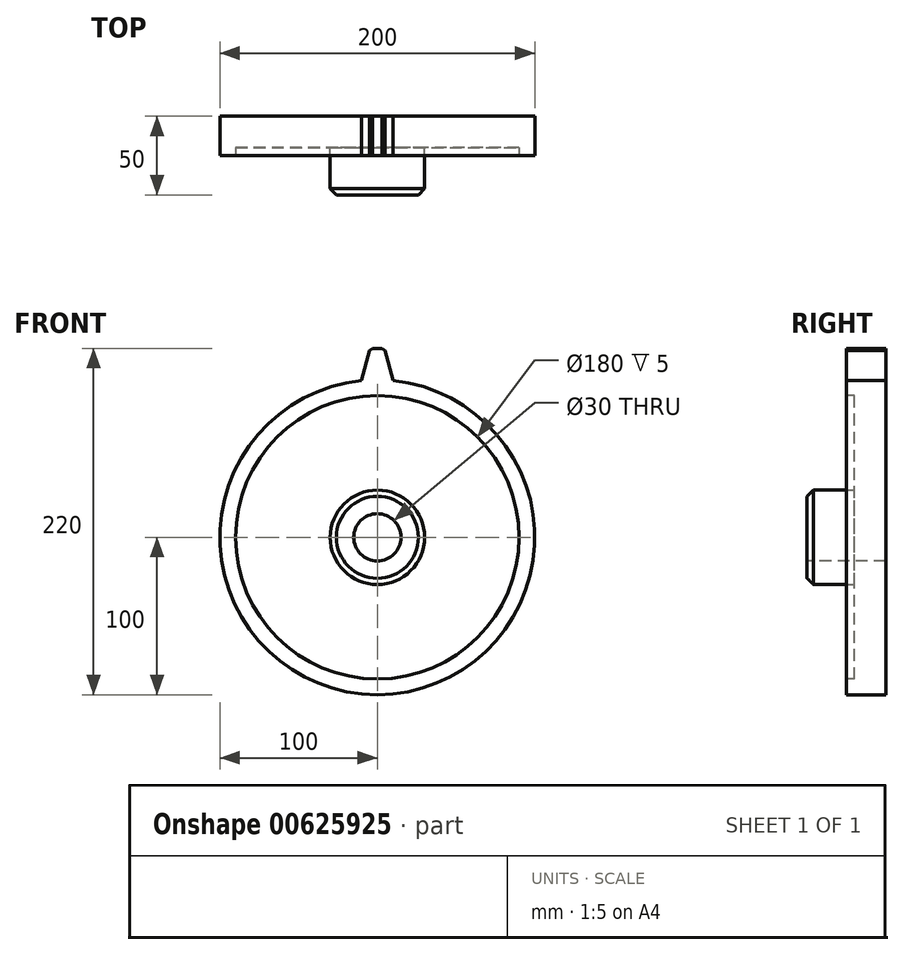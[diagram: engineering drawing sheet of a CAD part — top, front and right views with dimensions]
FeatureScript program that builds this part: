
annotation { "Feature Type Name" : "Feature", "Feature Type Description" : "" }
export const myFeature = defineFeature(function(context is Context, id is Id, definition is map)
    precondition{}
    {
        {
            var Q0;
            Q0=qCreatedBy(makeId("Front.planeOp"),FACE);
            var sketch = newSketch(context, id + "F0", { "sketchPlane" : qUnion([Q0])});
            skCircle(sketch, "E0", {"center": v(0, 0) * mm, "radius": 100 * mm});
            skSolve(sketch);
        }
        {
            var Q0;
            Q0=makeQuery(id+"F0.imprint","IMPRINT",FACE,{"disambiguationData":[TD([[makeQuery(id+"F0.imprint","IMPRINT",EDGE,{"derivedFrom":sQuery(id+"F0.wireOp",EDGE,"E0")}),1.0]])]});
            extrude(context, id + "F1", {"entities" : qUnion([Q0]), "depth" : 25 * mm, "offsetDistance" : 25 * mm});
        }
        {
            var Q0;
            Q0=qCreatedBy(makeId("Front.planeOp"),FACE);
            var sketch = newSketch(context, id + "F2", { "sketchPlane" : qUnion([Q0])});
            skLineSegment(sketch, "E1", {"start": v(-10, 99.5) * mm, "end": v(10, 99.5) * mm});
            skLineSegment(sketch, "E2", {"start": v(10, 99.5) * mm, "end": v(4.5, 120) * mm});
            skLineSegment(sketch, "E3", {"start": v(-4.5, 120) * mm, "end": v(4.5, 120) * mm});
            skLineSegment(sketch, "E4", {"start": v(-4.5, 120) * mm, "end": v(-10, 99.5) * mm});
            skSolve(sketch);
        }
        {
            var Q0;
            Q0 = qSketchRegion(id + "F2", true);
            extrude(context, id + "F3", {"entities" : qUnion([Q0]), "operationType" : NewBodyOperationType.ADD, "depth" : 25 * mm, "offsetDistance" : 25 * mm});
        }
        {
            var Q0;
            Q0=makeQuery(id+"F3.opExtrude","SWEPT_EDGE",EDGE,{"disambiguationData":[OSD([sQuery(id+"F2.wireOp",EDGE,"E3"),sQuery(id+"F2.wireOp",EDGE,"E4")])]});
            var Q1;
            Q1=makeQuery(id+"F3.opExtrude","SWEPT_EDGE",EDGE,{"disambiguationData":[OSD([sQuery(id+"F2.wireOp",EDGE,"E2"),sQuery(id+"F2.wireOp",EDGE,"E3")])]});
            chamfer(context, id + "F4", {"entities" : qUnion([Q0, Q1]), "width" : 2 * mm, "tangentPropagation" : true});
        }
        {
            var Q0;
            Q0=makeQuery(id+"F3.opExtrude","SWEPT_EDGE",EDGE,{"disambiguationData":[OSD([sQuery(id+"F2.wireOp",EDGE,"E1"),sQuery(id+"F2.wireOp",EDGE,"E2")])]});
            var Q1;
            Q1=makeQuery(id+"F3.opExtrude","SWEPT_EDGE",EDGE,{"disambiguationData":[OSD([sQuery(id+"F2.wireOp",EDGE,"E1"),sQuery(id+"F2.wireOp",EDGE,"E4")])]});
            fillet(context, id + "F5", {"entities" : qUnion([Q0, Q1]), "radius" : 5 * mm, "tangentPropagation" : true, "allowEdgeOverflow" : false});
        }
        {
            var Q0;
            {var subQ0=sQuery(id+"F2.wireOp",EDGE,"E4");var subQ1=sQuery(id+"F2.wireOp",EDGE,"E3");var subQ2=sQuery(id+"F2.wireOp",EDGE,"E2");var subQ3=sQuery(id+"F2.wireOp",EDGE,"E1");Q0=makeQuery(id+"FsMtaJyEFqotJcS_1.19.F3.boolean.opBoolean","MERGE",FACE,{"derivedFrom":[makeQuery(id+"FsMtaJyEFqotJcS_1.18.F3.boolean.opBoolean","MERGE",FACE,{"derivedFrom":[makeQuery(id+"FsMtaJyEFqotJcS_1.17.F3.boolean.opBoolean","MERGE",FACE,{"derivedFrom":[makeQuery(id+"FsMtaJyEFqotJcS_1.16.F3.boolean.opBoolean","MERGE",FACE,{"derivedFrom":[makeQuery(id+"FsMtaJyEFqotJcS_1.15.F3.boolean.opBoolean","MERGE",FACE,{"derivedFrom":[makeQuery(id+"FsMtaJyEFqotJcS_1.14.F3.boolean.opBoolean","MERGE",FACE,{"derivedFrom":[makeQuery(id+"FsMtaJyEFqotJcS_1.13.F3.boolean.opBoolean","MERGE",FACE,{"derivedFrom":[makeQuery(id+"FsMtaJyEFqotJcS_1.12.F3.boolean.opBoolean","MERGE",FACE,{"derivedFrom":[makeQuery(id+"FsMtaJyEFqotJcS_1.11.F3.boolean.opBoolean","MERGE",FACE,{"derivedFrom":[makeQuery(id+"FsMtaJyEFqotJcS_1.10.F3.boolean.opBoolean","MERGE",FACE,{"derivedFrom":[makeQuery(id+"FsMtaJyEFqotJcS_1.9.F3.boolean.opBoolean","MERGE",FACE,{"derivedFrom":[makeQuery(id+"FsMtaJyEFqotJcS_1.8.F3.boolean.opBoolean","MERGE",FACE,{"derivedFrom":[makeQuery(id+"FsMtaJyEFqotJcS_1.7.F3.boolean.opBoolean","MERGE",FACE,{"derivedFrom":[makeQuery(id+"FsMtaJyEFqotJcS_1.6.F3.boolean.opBoolean","MERGE",FACE,{"derivedFrom":[makeQuery(id+"FsMtaJyEFqotJcS_1.5.F3.boolean.opBoolean","MERGE",FACE,{"derivedFrom":[makeQuery(id+"FsMtaJyEFqotJcS_1.4.F3.boolean.opBoolean","MERGE",FACE,{"derivedFrom":[makeQuery(id+"FsMtaJyEFqotJcS_1.3.F3.boolean.opBoolean","MERGE",FACE,{"derivedFrom":[makeQuery(id+"FsMtaJyEFqotJcS_1.2.F3.boolean.opBoolean","MERGE",FACE,{"derivedFrom":[makeQuery(id+"FsMtaJyEFqotJcS_1.1.F3.boolean.opBoolean","MERGE",FACE,{"derivedFrom":[makeQuery(id+"F3.boolean.opBoolean","MERGE",FACE,{"derivedFrom":[makeQuery(id+"F1.opExtrude","CAP_FACE",FACE,{"disambiguationData":[OSD([sQuery(id+"F0.wireOp",EDGE,"E0")])],"isStart":false}),makeQuery(id+"F3.opExtrude","CAP_FACE",FACE,{"disambiguationData":[OSD([subQ3,subQ2,subQ1,subQ0])],"isStart":false})]}),makeQuery(id+"FsMtaJyEFqotJcS_1.1.F3.opExtrude","CAP_FACE",FACE,{"disambiguationData":[OSD([subQ3,subQ2,subQ1,subQ0])],"isStart":false})]}),makeQuery(id+"FsMtaJyEFqotJcS_1.2.F3.opExtrude","CAP_FACE",FACE,{"disambiguationData":[OSD([subQ3,subQ2,subQ1,subQ0])],"isStart":false})]}),makeQuery(id+"FsMtaJyEFqotJcS_1.3.F3.opExtrude","CAP_FACE",FACE,{"disambiguationData":[OSD([subQ3,subQ2,subQ1,subQ0])],"isStart":false})]}),makeQuery(id+"FsMtaJyEFqotJcS_1.4.F3.opExtrude","CAP_FACE",FACE,{"disambiguationData":[OSD([subQ3,subQ2,subQ1,subQ0])],"isStart":false})]}),makeQuery(id+"FsMtaJyEFqotJcS_1.5.F3.opExtrude","CAP_FACE",FACE,{"disambiguationData":[OSD([subQ3,subQ2,subQ1,subQ0])],"isStart":false})]}),makeQuery(id+"FsMtaJyEFqotJcS_1.6.F3.opExtrude","CAP_FACE",FACE,{"disambiguationData":[OSD([subQ3,subQ2,subQ1,subQ0])],"isStart":false})]}),makeQuery(id+"FsMtaJyEFqotJcS_1.7.F3.opExtrude","CAP_FACE",FACE,{"disambiguationData":[OSD([subQ3,subQ2,subQ1,subQ0])],"isStart":false})]}),makeQuery(id+"FsMtaJyEFqotJcS_1.8.F3.opExtrude","CAP_FACE",FACE,{"disambiguationData":[OSD([subQ3,subQ2,subQ1,subQ0])],"isStart":false})]}),makeQuery(id+"FsMtaJyEFqotJcS_1.9.F3.opExtrude","CAP_FACE",FACE,{"disambiguationData":[OSD([subQ3,subQ2,subQ1,subQ0])],"isStart":false})]}),makeQuery(id+"FsMtaJyEFqotJcS_1.10.F3.opExtrude","CAP_FACE",FACE,{"disambiguationData":[OSD([subQ3,subQ2,subQ1,subQ0])],"isStart":false})]}),makeQuery(id+"FsMtaJyEFqotJcS_1.11.F3.opExtrude","CAP_FACE",FACE,{"disambiguationData":[OSD([subQ3,subQ2,subQ1,subQ0])],"isStart":false})]}),makeQuery(id+"FsMtaJyEFqotJcS_1.12.F3.opExtrude","CAP_FACE",FACE,{"disambiguationData":[OSD([subQ3,subQ2,subQ1,subQ0])],"isStart":false})]}),makeQuery(id+"FsMtaJyEFqotJcS_1.13.F3.opExtrude","CAP_FACE",FACE,{"disambiguationData":[OSD([subQ3,subQ2,subQ1,subQ0])],"isStart":false})]}),makeQuery(id+"FsMtaJyEFqotJcS_1.14.F3.opExtrude","CAP_FACE",FACE,{"disambiguationData":[OSD([subQ3,subQ2,subQ1,subQ0])],"isStart":false})]}),makeQuery(id+"FsMtaJyEFqotJcS_1.15.F3.opExtrude","CAP_FACE",FACE,{"disambiguationData":[OSD([subQ3,subQ2,subQ1,subQ0])],"isStart":false})]}),makeQuery(id+"FsMtaJyEFqotJcS_1.16.F3.opExtrude","CAP_FACE",FACE,{"disambiguationData":[OSD([subQ3,subQ2,subQ1,subQ0])],"isStart":false})]}),makeQuery(id+"FsMtaJyEFqotJcS_1.17.F3.opExtrude","CAP_FACE",FACE,{"disambiguationData":[OSD([subQ3,subQ2,subQ1,subQ0])],"isStart":false})]}),makeQuery(id+"FsMtaJyEFqotJcS_1.18.F3.opExtrude","CAP_FACE",FACE,{"disambiguationData":[OSD([subQ3,subQ2,subQ1,subQ0])],"isStart":false})]}),makeQuery(id+"FsMtaJyEFqotJcS_1.19.F3.opExtrude","CAP_FACE",FACE,{"disambiguationData":[OSD([subQ3,subQ2,subQ1,subQ0])],"isStart":false})]});}
            var sketch = newSketch(context, id + "F6", { "sketchPlane" : qUnion([Q0])});
            skCircle(sketch, "E5", {"center": v(0, 0) * mm, "radius": 90 * mm});
            skSolve(sketch);
        }
        {
            var Q0;
            Q0 = qSketchRegion(id + "F6", true);
            extrude(context, id + "F7", {"entities" : qUnion([Q0]), "operationType" : NewBodyOperationType.REMOVE, "oppositeDirection" : true, "depth" : 5 * mm, "offsetDistance" : 25 * mm});
        }
        {
            var Q0;
            Q0=makeQuery(id+"F7.boolean.opBoolean","COPY",FACE,{"derivedFrom":makeQuery(id+"F7.opExtrude","CAP_FACE",FACE,{"disambiguationData":[OSD([sQuery(id+"F6.wireOp",EDGE,"E5")])],"isStart":false})});
            var sketch = newSketch(context, id + "F8", { "sketchPlane" : qUnion([Q0])});
            skCircle(sketch, "E6", {"center": v(0, 0) * mm, "radius": 30 * mm});
            skSolve(sketch);
        }
        {
            var Q0;
            Q0=makeQuery(id+"F8.imprint","IMPRINT",FACE,{"disambiguationData":[TD([[makeQuery(id+"F8.imprint","IMPRINT",EDGE,{"derivedFrom":sQuery(id+"F8.wireOp",EDGE,"E6")}),1.0]])]});
            extrude(context, id + "F9", {"entities" : qUnion([Q0]), "operationType" : NewBodyOperationType.ADD, "depth" : 30 * mm, "offsetDistance" : 25 * mm});
        }
        {
            var Q0;
            Q0=makeQuery(id+"F9.opExtrude","CAP_FACE",FACE,{"disambiguationData":[OSD([sQuery(id+"F8.wireOp",EDGE,"E6")])],"isStart":false});
            var sketch = newSketch(context, id + "F10", { "sketchPlane" : qUnion([Q0])});
            skCircle(sketch, "E7", {"center": v(0, 0) * mm, "radius": 15 * mm});
            skSolve(sketch);
        }
        {
            var Q0;
            Q0 = qSketchRegion(id + "F10", true);
            extrude(context, id + "F11", {"entities" : qUnion([Q0]), "operationType" : NewBodyOperationType.REMOVE, "endBound" : BoundingType.THROUGH_ALL, "oppositeDirection" : true, "depth" : 25 * mm, "offsetDistance" : 25 * mm});
        }
        {
            var Q0;
            Q0=makeQuery(id+"F9.opExtrude","CAP_EDGE",EDGE,{"disambiguationData":[OSD([sQuery(id+"F8.wireOp",EDGE,"E6")])],"isStart":false});
            var Q1;
            Q1=makeQuery(id+"F11.boolean.opBoolean","COPY",EDGE,{"derivedFrom":makeQuery(id+"F11.opExtrude","CAP_EDGE",EDGE,{"disambiguationData":[OSD([sQuery(id+"F10.wireOp",EDGE,"E7")])],"isStart":true})});
            chamfer(context, id + "F12", {"entities" : qUnion([Q0, Q1]), "width" : 4 * mm, "tangentPropagation" : true});
        }
    });
